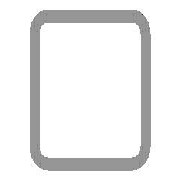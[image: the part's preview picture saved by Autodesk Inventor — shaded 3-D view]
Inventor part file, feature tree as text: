
AUTODESK INVENTOR PART (.ipt)
format: ipt  version: 2024 (Build 280153000, 153)  size: 128,512 bytes
history: native  units: mm (DEFAULTED — no unit token found)
features: other x4, extrude x1, sketch x1, plane x1
ambient origin geometry x8: Origin, YZ Plane, XZ Plane, XY Plane, X Axis, Y Axis, Z Axis, Center Point
bodies: Solid1 (feature_tree)
feature tree (7):
  parser-record x1  (decoder bookkeeping rows leaked as tree rows — omitted from the tree; the rows remain in map.json)
  other  "Driven Length"
  other  "Plano inicial"
  other  "Plano final"
  extrude  "Cuerpo"  TaperAngle=0.0deg  [1 undecoded]
  sketch  "Sketch3"  dims[d3=2200.0mm d4=0.0mm d10=50.8mm d11=50.8mm d12=3.175mm d13=-0.0mm d14=2200.0mm d15=25.4mm d16=25.4mm d17=6.35mm d18=90.0deg d19=2200.0mm]
  plane  "Work Plane3"
note: 1 required parameter value undecoded (feature->parameter linkage not recoverable at this tier; creation-order binding heuristic only, values carry confidence <= 0.55)
